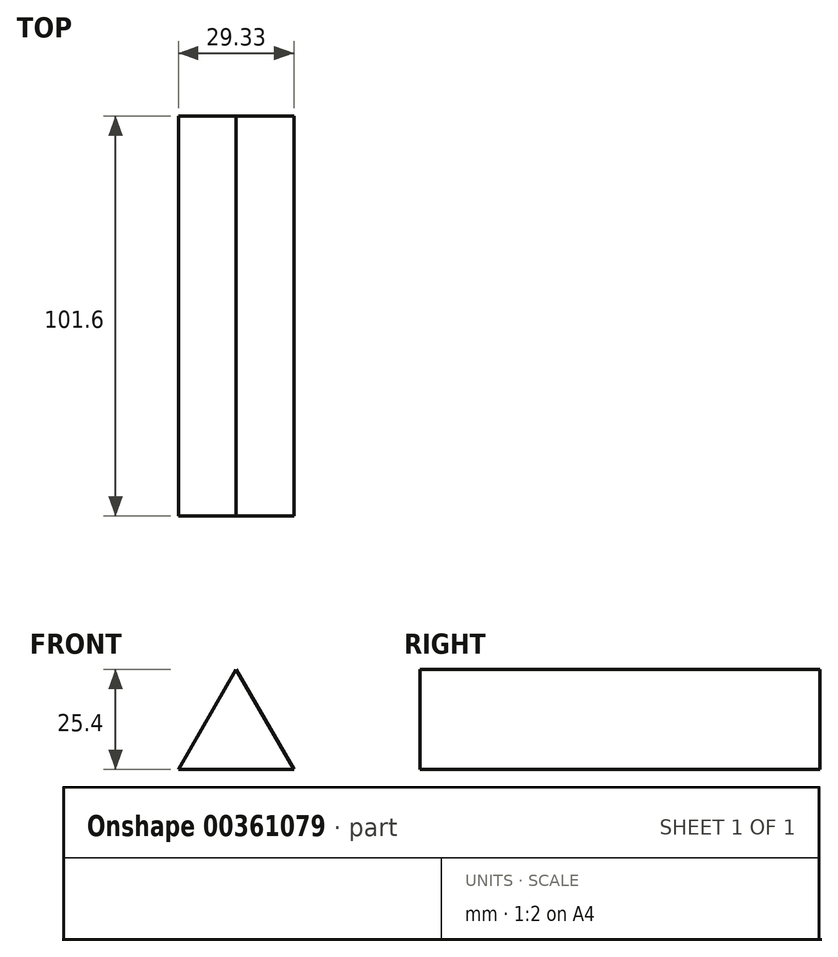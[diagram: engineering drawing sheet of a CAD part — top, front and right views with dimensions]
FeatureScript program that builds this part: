
annotation { "Feature Type Name" : "Feature", "Feature Type Description" : "" }
export const myFeature = defineFeature(function(context is Context, id is Id, definition is map)
    precondition{}
    {
        {
            var Q0;
            Q0=qCreatedBy(makeId("Front.planeOp"),FACE);
            var sketch = newSketch(context, id + "F0", { "sketchPlane" : qUnion([Q0])});
            skLineSegment(sketch, "E0", {"start": v(20.74, -51.83) * mm, "end": v(50.07, -51.83) * mm});
            skLineSegment(sketch, "E1", {"start": v(50.07, -51.83) * mm, "end": v(35.4, -26.43) * mm});
            skLineSegment(sketch, "E2", {"start": v(35.4, -26.43) * mm, "end": v(20.74, -51.83) * mm});
            skSolve(sketch);
        }
        {
            var Q0;
            Q0=makeQuery(id+"F0.imprint","IMPRINT",FACE,{"disambiguationData":[TD([[makeQuery(id+"F0.imprint","IMPRINT",EDGE,{"derivedFrom":sQuery(id+"F0.wireOp",EDGE,"E0")}),1.0]])]});
            extrude(context, id + "F1", {"entities" : qUnion([Q0]), "depth" : 101.6 * mm});
        }
    });
